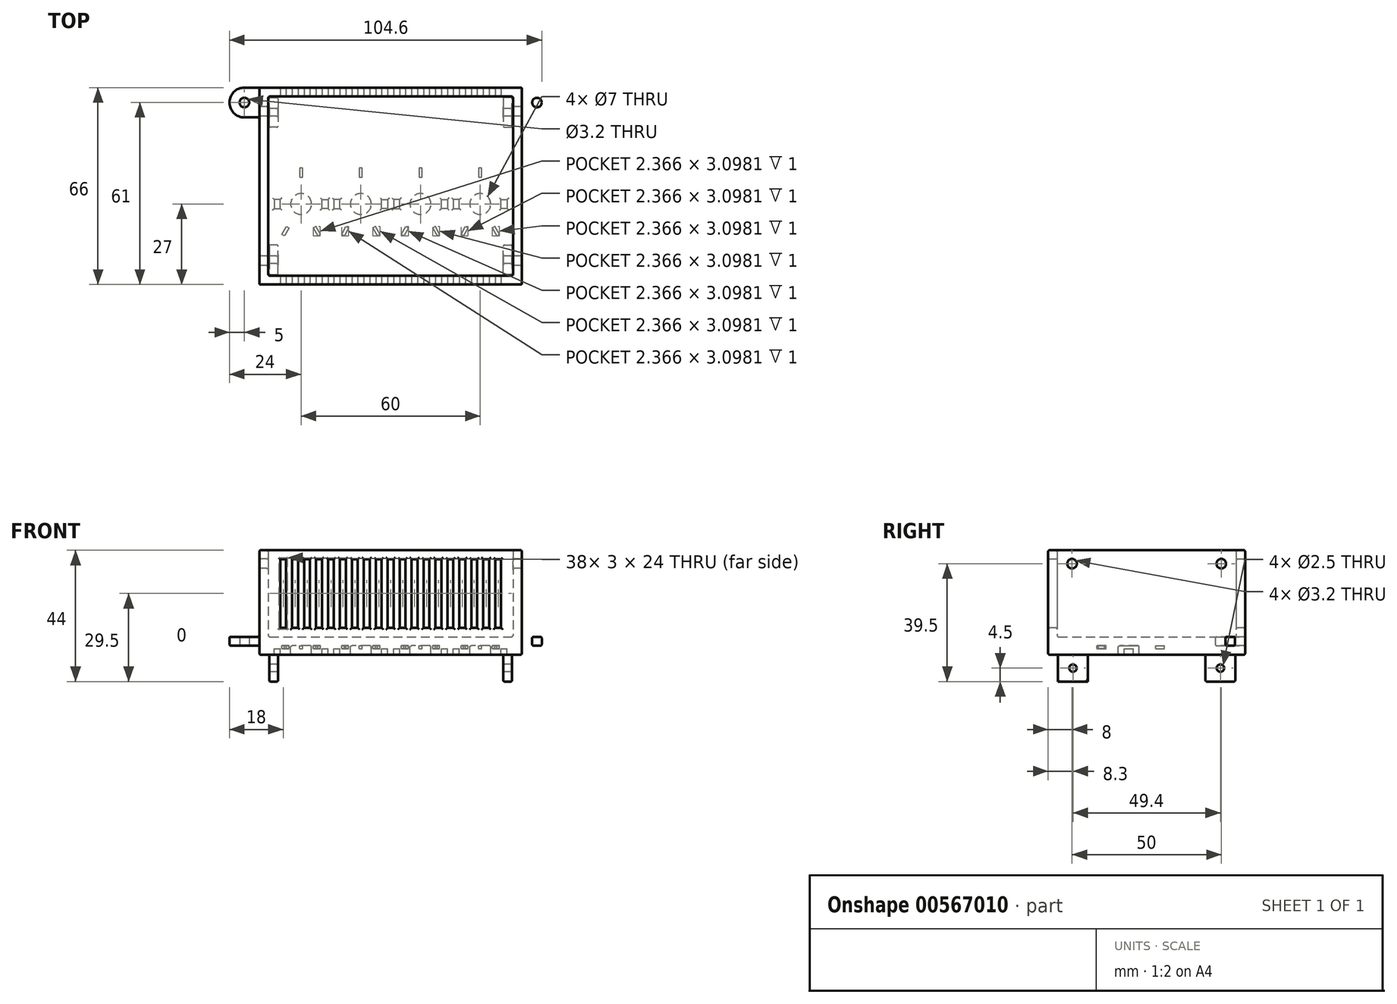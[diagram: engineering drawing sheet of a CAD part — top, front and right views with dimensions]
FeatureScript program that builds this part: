
annotation { "Feature Type Name" : "Feature", "Feature Type Description" : "" }
export const myFeature = defineFeature(function(context is Context, id is Id, definition is map)
    precondition{}
    {
        {
            assignVariable(context, id + "F0", {"name" : "wallthickness", "anyValue" : 3 * mm});
        }
        {
            assignVariable(context, id + "F1", {"name" : "width", "anyValue" : 82 * mm});
        }
        {
            assignVariable(context, id + "F2", {"name" : "height", "anyValue" : 60 * mm});
        }
        {
            assignVariable(context, id + "F3", {"name" : "depth", "anyValue" : 29 * mm});
        }
        {
            assignVariable(context, id + "F4", {"name" : "filletrad", "anyValue" : 0.5 * mm});
        }
        {
            var Q0;
            Q0=qCreatedBy(makeId("Top.planeOp"),FACE);
            var sketch = newSketch(context, id + "F5", { "sketchPlane" : qUnion([Q0])});
            skLineSegment(sketch, "E0", {"start": v(0, 0) * mm, "end": v(82, 0) * mm});
            skLineSegment(sketch, "E1", {"start": v(82, 0) * mm, "end": v(82, -60) * mm});
            skLineSegment(sketch, "E2", {"start": v(82, -60) * mm, "end": v(0, -60) * mm});
            skLineSegment(sketch, "E3", {"start": v(0, -60) * mm, "end": v(0, 0) * mm});
            skLineSegment(sketch, "E4.0", {"start": v(-3, 3) * mm, "end": v(85, 3) * mm});
            skLineSegment(sketch, "E4.1", {"start": v(-3, -63) * mm, "end": v(-3, 3) * mm});
            skLineSegment(sketch, "E4.2", {"start": v(85, -63) * mm, "end": v(-3, -63) * mm});
            skLineSegment(sketch, "E4.3", {"start": v(85, 3) * mm, "end": v(85, -63) * mm});
            skLineSegment(sketch, "E5", {"start": v(0.3, -0.3) * mm, "end": v(3.3, -0.3) * mm});
            skLineSegment(sketch, "E6", {"start": v(3.3, -0.3) * mm, "end": v(3.3, -10.3) * mm});
            skLineSegment(sketch, "E7", {"start": v(3.3, -10.3) * mm, "end": v(0.3, -10.3) * mm});
            skLineSegment(sketch, "E8", {"start": v(0.3, -10.3) * mm, "end": v(0.3, -0.3) * mm});
            skLineSegment(sketch, "E9", {"start": v(-3, -30) * mm, "end": v(85, -30) * mm, "construction": true});
            skLineSegment(sketch, "E10.MirrorCS", {"start": v(3.3, -59.7) * mm, "end": v(3.3, -49.7) * mm});
            skLineSegment(sketch, "E11.MirrorCS", {"start": v(3.3, -49.7) * mm, "end": v(0.3, -49.7) * mm});
            skLineSegment(sketch, "E12.MirrorCS", {"start": v(0.3, -59.7) * mm, "end": v(3.3, -59.7) * mm});
            skLineSegment(sketch, "E13.MirrorCS", {"start": v(0.3, -49.7) * mm, "end": v(0.3, -59.7) * mm});
            skCircle(sketch, "E14", {"center": v(11, -36) * mm, "radius": 9 * mm, "construction": true});
            skCircle(sketch, "E15", {"center": v(11, -36) * mm, "radius": 3.5 * mm});
            skLineSegment(sketch, "E16", {"start": v(18, -34.5) * mm, "end": v(20, -34.5) * mm});
            skLineSegment(sketch, "E17", {"start": v(20, -34.5) * mm, "end": v(20, -37.5) * mm});
            skLineSegment(sketch, "E18", {"start": v(20, -37.5) * mm, "end": v(18, -37.5) * mm});
            skLineSegment(sketch, "E19", {"start": v(18, -37.5) * mm, "end": v(18, -34.5) * mm});
            skLineSegment(sketch, "E20", {"start": v(11, -36) * mm, "end": v(11, -30) * mm, "construction": true});
            skLineSegment(sketch, "E21.MirrorCS", {"start": v(2, -37.5) * mm, "end": v(4, -37.5) * mm});
            skLineSegment(sketch, "E22.MirrorCS", {"start": v(2, -34.5) * mm, "end": v(2, -37.5) * mm});
            skLineSegment(sketch, "E23.MirrorCS", {"start": v(4, -37.5) * mm, "end": v(4, -34.5) * mm});
            skLineSegment(sketch, "E24.MirrorCS", {"start": v(4, -34.5) * mm, "end": v(2, -34.5) * mm});
            skLineSegment(sketch, "E25.1.0.0", {"start": v(22, -37.5) * mm, "end": v(24, -37.5) * mm});
            skLineSegment(sketch, "E25.1.0.1", {"start": v(22, -34.5) * mm, "end": v(22, -37.5) * mm});
            skLineSegment(sketch, "E25.1.0.2", {"start": v(24, -34.5) * mm, "end": v(22, -34.5) * mm});
            skLineSegment(sketch, "E25.1.0.3", {"start": v(24, -37.5) * mm, "end": v(24, -34.5) * mm});
            skLineSegment(sketch, "E25.1.0.4", {"start": v(40, -34.5) * mm, "end": v(40, -37.5) * mm});
            skCircle(sketch, "E25.1.0.5", {"center": v(31, -36) * mm, "radius": 3.5 * mm});
            skLineSegment(sketch, "E25.1.0.6", {"start": v(38, -34.5) * mm, "end": v(40, -34.5) * mm});
            skLineSegment(sketch, "E25.1.0.7", {"start": v(38, -37.5) * mm, "end": v(38, -34.5) * mm});
            skLineSegment(sketch, "E25.1.0.8", {"start": v(31, -36) * mm, "end": v(31, -30) * mm, "construction": true});
            skLineSegment(sketch, "E25.1.0.9", {"start": v(40, -37.5) * mm, "end": v(38, -37.5) * mm});
            skLineSegment(sketch, "E25.2.0.0", {"start": v(42, -37.5) * mm, "end": v(44, -37.5) * mm});
            skLineSegment(sketch, "E25.2.0.1", {"start": v(42, -34.5) * mm, "end": v(42, -37.5) * mm});
            skLineSegment(sketch, "E25.2.0.2", {"start": v(44, -34.5) * mm, "end": v(42, -34.5) * mm});
            skLineSegment(sketch, "E25.2.0.3", {"start": v(44, -37.5) * mm, "end": v(44, -34.5) * mm});
            skLineSegment(sketch, "E25.2.0.4", {"start": v(60, -34.5) * mm, "end": v(60, -37.5) * mm});
            skCircle(sketch, "E25.2.0.5", {"center": v(51, -36) * mm, "radius": 3.5 * mm});
            skLineSegment(sketch, "E25.2.0.6", {"start": v(58, -34.5) * mm, "end": v(60, -34.5) * mm});
            skLineSegment(sketch, "E25.2.0.7", {"start": v(58, -37.5) * mm, "end": v(58, -34.5) * mm});
            skLineSegment(sketch, "E25.2.0.8", {"start": v(51, -36) * mm, "end": v(51, -30) * mm, "construction": true});
            skLineSegment(sketch, "E25.2.0.9", {"start": v(60, -37.5) * mm, "end": v(58, -37.5) * mm});
            skLineSegment(sketch, "E25.3.0.0", {"start": v(62, -37.5) * mm, "end": v(64, -37.5) * mm});
            skLineSegment(sketch, "E25.3.0.1", {"start": v(62, -34.5) * mm, "end": v(62, -37.5) * mm});
            skLineSegment(sketch, "E25.3.0.2", {"start": v(64, -34.5) * mm, "end": v(62, -34.5) * mm});
            skLineSegment(sketch, "E25.3.0.3", {"start": v(64, -37.5) * mm, "end": v(64, -34.5) * mm});
            skLineSegment(sketch, "E25.3.0.4", {"start": v(80, -34.5) * mm, "end": v(80, -37.5) * mm});
            skCircle(sketch, "E25.3.0.5", {"center": v(71, -36) * mm, "radius": 3.5 * mm});
            skLineSegment(sketch, "E25.3.0.6", {"start": v(78, -34.5) * mm, "end": v(80, -34.5) * mm});
            skLineSegment(sketch, "E25.3.0.7", {"start": v(78, -37.5) * mm, "end": v(78, -34.5) * mm});
            skLineSegment(sketch, "E25.3.0.8", {"start": v(71, -36) * mm, "end": v(71, -30) * mm, "construction": true});
            skLineSegment(sketch, "E25.3.0.9", {"start": v(80, -37.5) * mm, "end": v(78, -37.5) * mm});
            skLineSegment(sketch, "E25.direction1", {"start": v(2, -37.5) * mm, "end": v(22, -37.5) * mm, "construction": true});
            skLineSegment(sketch, "E26", {"start": v(41, 3) * mm, "end": v(41, -60) * mm, "construction": true});
            skLineSegment(sketch, "E27.MirrorCS", {"start": v(81.7, -49.7) * mm, "end": v(81.7, -59.7) * mm});
            skLineSegment(sketch, "E28.MirrorCS", {"start": v(78.7, -49.7) * mm, "end": v(81.7, -49.7) * mm});
            skLineSegment(sketch, "E29.MirrorCS", {"start": v(81.7, -59.7) * mm, "end": v(78.7, -59.7) * mm});
            skLineSegment(sketch, "E30.MirrorCS", {"start": v(78.7, -59.7) * mm, "end": v(78.7, -49.7) * mm});
            skLineSegment(sketch, "E31.MirrorCS", {"start": v(81.7, -10.3) * mm, "end": v(81.7, -0.3) * mm});
            skLineSegment(sketch, "E32.MirrorCS", {"start": v(78.7, -0.3) * mm, "end": v(78.7, -10.3) * mm});
            skLineSegment(sketch, "E33.MirrorCS", {"start": v(81.7, -0.3) * mm, "end": v(78.7, -0.3) * mm});
            skLineSegment(sketch, "E34.MirrorCS", {"start": v(78.7, -10.3) * mm, "end": v(81.7, -10.3) * mm});
            skLineSegment(sketch, "E35", {"start": v(11, -36) * mm, "end": v(5, -46.4) * mm, "construction": true});
            skLineSegment(sketch, "E36", {"start": v(5, -46.4) * mm, "end": v(4.57, -46.14) * mm});
            skLineSegment(sketch, "E37", {"start": v(4.57, -46.14) * mm, "end": v(6.07, -43.54) * mm});
            skLineSegment(sketch, "E38", {"start": v(6.07, -43.54) * mm, "end": v(6.93, -44.04) * mm});
            skLineSegment(sketch, "E39", {"start": v(6.93, -44.04) * mm, "end": v(5.43, -46.64) * mm});
            skLineSegment(sketch, "E40", {"start": v(5.43, -46.64) * mm, "end": v(5, -46.4) * mm});
            skLineSegment(sketch, "E41.MirrorCS", {"start": v(16.57, -46.64) * mm, "end": v(17, -46.4) * mm});
            skLineSegment(sketch, "E42.MirrorCS", {"start": v(17, -46.4) * mm, "end": v(17.43, -46.14) * mm});
            skLineSegment(sketch, "E43.MirrorCS", {"start": v(15.07, -44.04) * mm, "end": v(16.57, -46.64) * mm});
            skLineSegment(sketch, "E44.MirrorCS", {"start": v(15.93, -43.54) * mm, "end": v(15.07, -44.04) * mm});
            skLineSegment(sketch, "E45.MirrorCS", {"start": v(17.43, -46.14) * mm, "end": v(15.93, -43.54) * mm});
            skLineSegment(sketch, "E46", {"start": v(11, -30) * mm, "end": v(11, -27) * mm, "construction": true});
            skLineSegment(sketch, "E47", {"start": v(11, -27) * mm, "end": v(11.5, -27) * mm});
            skLineSegment(sketch, "E48", {"start": v(11.5, -27) * mm, "end": v(11.5, -24) * mm});
            skLineSegment(sketch, "E49", {"start": v(11.5, -24) * mm, "end": v(10.5, -24) * mm});
            skLineSegment(sketch, "E50", {"start": v(10.5, -24) * mm, "end": v(10.5, -27) * mm});
            skLineSegment(sketch, "E51", {"start": v(10.5, -27) * mm, "end": v(11, -27) * mm});
            skLineSegment(sketch, "E52.1.0.0", {"start": v(31.5, -27) * mm, "end": v(31.5, -24) * mm});
            skLineSegment(sketch, "E52.1.0.1", {"start": v(30.5, -27) * mm, "end": v(31, -27) * mm});
            skLineSegment(sketch, "E52.1.0.2", {"start": v(30.5, -24) * mm, "end": v(30.5, -27) * mm});
            skLineSegment(sketch, "E52.1.0.3", {"start": v(31, -27) * mm, "end": v(31.5, -27) * mm});
            skLineSegment(sketch, "E52.1.0.4", {"start": v(31.5, -24) * mm, "end": v(30.5, -24) * mm});
            skLineSegment(sketch, "E52.1.0.5", {"start": v(37.43, -46.14) * mm, "end": v(35.93, -43.54) * mm});
            skLineSegment(sketch, "E52.1.0.6", {"start": v(35.07, -44.04) * mm, "end": v(36.57, -46.64) * mm});
            skLineSegment(sketch, "E52.1.0.7", {"start": v(26.93, -44.04) * mm, "end": v(25.43, -46.64) * mm});
            skLineSegment(sketch, "E52.1.0.8", {"start": v(24.57, -46.14) * mm, "end": v(26.07, -43.54) * mm});
            skLineSegment(sketch, "E52.1.0.9", {"start": v(36.57, -46.64) * mm, "end": v(37, -46.4) * mm});
            skLineSegment(sketch, "E52.1.0.10", {"start": v(35.93, -43.54) * mm, "end": v(35.07, -44.04) * mm});
            skLineSegment(sketch, "E52.1.0.11", {"start": v(37, -46.4) * mm, "end": v(37.43, -46.14) * mm});
            skLineSegment(sketch, "E52.1.0.12", {"start": v(26.07, -43.54) * mm, "end": v(26.93, -44.04) * mm});
            skLineSegment(sketch, "E52.1.0.13", {"start": v(25.43, -46.64) * mm, "end": v(25, -46.4) * mm});
            skLineSegment(sketch, "E52.1.0.14", {"start": v(25, -46.4) * mm, "end": v(24.57, -46.14) * mm});
            skLineSegment(sketch, "E52.2.0.0", {"start": v(51.5, -27) * mm, "end": v(51.5, -24) * mm});
            skLineSegment(sketch, "E52.2.0.1", {"start": v(50.5, -27) * mm, "end": v(51, -27) * mm});
            skLineSegment(sketch, "E52.2.0.2", {"start": v(50.5, -24) * mm, "end": v(50.5, -27) * mm});
            skLineSegment(sketch, "E52.2.0.3", {"start": v(51, -27) * mm, "end": v(51.5, -27) * mm});
            skLineSegment(sketch, "E52.2.0.4", {"start": v(51.5, -24) * mm, "end": v(50.5, -24) * mm});
            skLineSegment(sketch, "E52.2.0.5", {"start": v(57.43, -46.14) * mm, "end": v(55.93, -43.54) * mm});
            skLineSegment(sketch, "E52.2.0.6", {"start": v(55.07, -44.04) * mm, "end": v(56.57, -46.64) * mm});
            skLineSegment(sketch, "E52.2.0.7", {"start": v(46.93, -44.04) * mm, "end": v(45.43, -46.64) * mm});
            skLineSegment(sketch, "E52.2.0.8", {"start": v(44.57, -46.14) * mm, "end": v(46.07, -43.54) * mm});
            skLineSegment(sketch, "E52.2.0.9", {"start": v(56.57, -46.64) * mm, "end": v(57, -46.4) * mm});
            skLineSegment(sketch, "E52.2.0.10", {"start": v(55.93, -43.54) * mm, "end": v(55.07, -44.04) * mm});
            skLineSegment(sketch, "E52.2.0.11", {"start": v(57, -46.4) * mm, "end": v(57.43, -46.14) * mm});
            skLineSegment(sketch, "E52.2.0.12", {"start": v(46.07, -43.54) * mm, "end": v(46.93, -44.04) * mm});
            skLineSegment(sketch, "E52.2.0.13", {"start": v(45.43, -46.64) * mm, "end": v(45, -46.4) * mm});
            skLineSegment(sketch, "E52.2.0.14", {"start": v(45, -46.4) * mm, "end": v(44.57, -46.14) * mm});
            skLineSegment(sketch, "E52.3.0.0", {"start": v(71.5, -27) * mm, "end": v(71.5, -24) * mm});
            skLineSegment(sketch, "E52.3.0.1", {"start": v(70.5, -27) * mm, "end": v(71, -27) * mm});
            skLineSegment(sketch, "E52.3.0.2", {"start": v(70.5, -24) * mm, "end": v(70.5, -27) * mm});
            skLineSegment(sketch, "E52.3.0.3", {"start": v(71, -27) * mm, "end": v(71.5, -27) * mm});
            skLineSegment(sketch, "E52.3.0.4", {"start": v(71.5, -24) * mm, "end": v(70.5, -24) * mm});
            skLineSegment(sketch, "E52.3.0.5", {"start": v(77.43, -46.14) * mm, "end": v(75.93, -43.54) * mm});
            skLineSegment(sketch, "E52.3.0.6", {"start": v(75.07, -44.04) * mm, "end": v(76.57, -46.64) * mm});
            skLineSegment(sketch, "E52.3.0.7", {"start": v(66.93, -44.04) * mm, "end": v(65.43, -46.64) * mm});
            skLineSegment(sketch, "E52.3.0.8", {"start": v(64.57, -46.14) * mm, "end": v(66.07, -43.54) * mm});
            skLineSegment(sketch, "E52.3.0.9", {"start": v(76.57, -46.64) * mm, "end": v(77, -46.4) * mm});
            skLineSegment(sketch, "E52.3.0.10", {"start": v(75.93, -43.54) * mm, "end": v(75.07, -44.04) * mm});
            skLineSegment(sketch, "E52.3.0.11", {"start": v(77, -46.4) * mm, "end": v(77.43, -46.14) * mm});
            skLineSegment(sketch, "E52.3.0.12", {"start": v(66.07, -43.54) * mm, "end": v(66.93, -44.04) * mm});
            skLineSegment(sketch, "E52.3.0.13", {"start": v(65.43, -46.64) * mm, "end": v(65, -46.4) * mm});
            skLineSegment(sketch, "E52.3.0.14", {"start": v(65, -46.4) * mm, "end": v(64.57, -46.14) * mm});
            skLineSegment(sketch, "E52.direction1", {"start": v(4.57, -46.14) * mm, "end": v(24.57, -46.14) * mm, "construction": true});
            skLineSegment(sketch, "E53", {"start": v(-3, 3) * mm, "end": v(-8, 3) * mm});
            skLineSegment(sketch, "E54", {"start": v(-8, 3) * mm, "end": v(-8, -7) * mm, "construction": true});
            skLineSegment(sketch, "E55", {"start": v(-8, -7) * mm, "end": v(-3, -7) * mm});
            skArc(sketch, "E56", {"start": v(-8, 3) * mm, "mid": v(-13, -2) * mm, "end": v(-8, -7) * mm});
            skCircle(sketch, "E57", {"center": v(-8, -2) * mm, "radius": 1.6 * mm});
            skCircle(sketch, "E58.MirrorC", {"center": v(90, -2) * mm, "radius": 1.6 * mm});
            skArc(sketch, "E59.MirrorCS", {"start": v(90, 3) * mm, "mid": v(95, -2) * mm, "end": v(90, -7) * mm});
            skLineSegment(sketch, "E60.MirrorCS", {"start": v(90, -7) * mm, "end": v(85, -7) * mm});
            skLineSegment(sketch, "E61.MirrorCS", {"start": v(85, 3) * mm, "end": v(90, 3) * mm});
            skLineSegment(sketch, "E62.MirrorCS", {"start": v(90, 3) * mm, "end": v(90, -7) * mm, "construction": true});
            skSolve(sketch);
        }
        {
            var Q0;
            Q0=makeQuery(id+"F5.imprint","IMPRINT",FACE,{"disambiguationData":[TD([[makeQuery(id+"F5.imprint","IMPRINT",EDGE,{"derivedFrom":sQuery(id+"F5.wireOp",EDGE,"E0")}),1.0]])]});
            extrude(context, id + "F6", {"entities" : qUnion([Q0]), "depth" : getVariable(context, 'depth') + getVariable(context, 'wallthickness'), "offsetDistance" : 25 * mm});
        }
        {
            var Q0;
            Q0=makeQuery(id+"F5.imprint","IMPRINT",FACE,{"disambiguationData":[TD([[makeQuery(id+"F5.imprint","IMPRINT",EDGE,{"derivedFrom":sQuery(id+"F5.wireOp",EDGE,"E0")}),-1.0]])]});
            var Q1;
            Q1=makeQuery(id+"F5.imprint","IMPRINT",FACE,{"disambiguationData":[TD([[makeQuery(id+"F5.imprint","IMPRINT",EDGE,{"derivedFrom":sQuery(id+"F5.wireOp",EDGE,"E5")}),-1.0]])]});
            var Q2;
            Q2=makeQuery(id+"F5.imprint","IMPRINT",FACE,{"disambiguationData":[TD([[makeQuery(id+"F5.imprint","IMPRINT",EDGE,{"derivedFrom":sQuery(id+"F5.wireOp",EDGE,"E10.MirrorCS")}),1.0]])]});
            var Q3;
            Q3=makeQuery(id+"F5.imprint","IMPRINT",FACE,{"disambiguationData":[TD([[makeQuery(id+"F5.imprint","IMPRINT",EDGE,{"derivedFrom":sQuery(id+"F5.wireOp",EDGE,"E21.MirrorCS")}),1.0]])]});
            var Q4;
            Q4=makeQuery(id+"F5.imprint","IMPRINT",FACE,{"disambiguationData":[TD([[makeQuery(id+"F5.imprint","IMPRINT",EDGE,{"derivedFrom":sQuery(id+"F5.wireOp",EDGE,"E15")}),1.0]])]});
            var Q5;
            Q5=makeQuery(id+"F5.imprint","IMPRINT",FACE,{"disambiguationData":[TD([[makeQuery(id+"F5.imprint","IMPRINT",EDGE,{"derivedFrom":sQuery(id+"F5.wireOp",EDGE,"E16")}),-1.0]])]});
            var Q6;
            Q6=makeQuery(id+"F5.imprint","IMPRINT",FACE,{"disambiguationData":[TD([[makeQuery(id+"F5.imprint","IMPRINT",EDGE,{"derivedFrom":sQuery(id+"F5.wireOp",EDGE,"E25.1.0.0")}),1.0]])]});
            var Q7;
            Q7=makeQuery(id+"F5.imprint","IMPRINT",FACE,{"disambiguationData":[TD([[makeQuery(id+"F5.imprint","IMPRINT",EDGE,{"derivedFrom":sQuery(id+"F5.wireOp",EDGE,"E25.1.0.5")}),1.0]])]});
            var Q8;
            Q8=makeQuery(id+"F5.imprint","IMPRINT",FACE,{"disambiguationData":[TD([[makeQuery(id+"F5.imprint","IMPRINT",EDGE,{"derivedFrom":sQuery(id+"F5.wireOp",EDGE,"E25.1.0.4")}),-1.0]])]});
            var Q9;
            Q9=makeQuery(id+"F5.imprint","IMPRINT",FACE,{"disambiguationData":[TD([[makeQuery(id+"F5.imprint","IMPRINT",EDGE,{"derivedFrom":sQuery(id+"F5.wireOp",EDGE,"E25.2.0.0")}),1.0]])]});
            var Q10;
            Q10=makeQuery(id+"F5.imprint","IMPRINT",FACE,{"disambiguationData":[TD([[makeQuery(id+"F5.imprint","IMPRINT",EDGE,{"derivedFrom":sQuery(id+"F5.wireOp",EDGE,"E25.2.0.5")}),1.0]])]});
            var Q11;
            Q11=makeQuery(id+"F5.imprint","IMPRINT",FACE,{"disambiguationData":[TD([[makeQuery(id+"F5.imprint","IMPRINT",EDGE,{"derivedFrom":sQuery(id+"F5.wireOp",EDGE,"E25.3.0.0")}),1.0]])]});
            var Q12;
            Q12=makeQuery(id+"F5.imprint","IMPRINT",FACE,{"disambiguationData":[TD([[makeQuery(id+"F5.imprint","IMPRINT",EDGE,{"derivedFrom":sQuery(id+"F5.wireOp",EDGE,"E25.2.0.4")}),-1.0]])]});
            var Q13;
            Q13=makeQuery(id+"F5.imprint","IMPRINT",FACE,{"disambiguationData":[TD([[makeQuery(id+"F5.imprint","IMPRINT",EDGE,{"derivedFrom":sQuery(id+"F5.wireOp",EDGE,"E25.3.0.5")}),1.0]])]});
            var Q14;
            Q14=makeQuery(id+"F5.imprint","IMPRINT",FACE,{"disambiguationData":[TD([[makeQuery(id+"F5.imprint","IMPRINT",EDGE,{"derivedFrom":sQuery(id+"F5.wireOp",EDGE,"E25.3.0.4")}),-1.0]])]});
            var Q15;
            Q15=makeQuery(id+"F5.imprint","IMPRINT",FACE,{"disambiguationData":[TD([[makeQuery(id+"F5.imprint","IMPRINT",EDGE,{"derivedFrom":sQuery(id+"F5.wireOp",EDGE,"E31.MirrorCS")}),1.0]])]});
            var Q16;
            Q16=makeQuery(id+"F5.imprint","IMPRINT",FACE,{"disambiguationData":[TD([[makeQuery(id+"F5.imprint","IMPRINT",EDGE,{"derivedFrom":sQuery(id+"F5.wireOp",EDGE,"E27.MirrorCS")}),-1.0]])]});
            var Q17;
            Q17=makeQuery(id+"F5.imprint","IMPRINT",FACE,{"disambiguationData":[TD([[makeQuery(id+"F5.imprint","IMPRINT",EDGE,{"derivedFrom":sQuery(id+"F5.wireOp",EDGE,"E36")}),-1.0]])]});
            var Q18;
            Q18=makeQuery(id+"F5.imprint","IMPRINT",FACE,{"disambiguationData":[TD([[makeQuery(id+"F5.imprint","IMPRINT",EDGE,{"derivedFrom":sQuery(id+"F5.wireOp",EDGE,"E41.MirrorCS")}),1.0]])]});
            var Q19;
            Q19=makeQuery(id+"F5.imprint","IMPRINT",FACE,{"disambiguationData":[TD([[makeQuery(id+"F5.imprint","IMPRINT",EDGE,{"derivedFrom":sQuery(id+"F5.wireOp",EDGE,"E47")}),1.0]])]});
            var Q20;
            Q20=makeQuery(id+"F5.imprint","IMPRINT",FACE,{"disambiguationData":[TD([[makeQuery(id+"F5.imprint","IMPRINT",EDGE,{"derivedFrom":sQuery(id+"F5.wireOp",EDGE,"E52.1.0.5")}),1.0]])]});
            var Q21;
            Q21=makeQuery(id+"F5.imprint","IMPRINT",FACE,{"disambiguationData":[TD([[makeQuery(id+"F5.imprint","IMPRINT",EDGE,{"derivedFrom":sQuery(id+"F5.wireOp",EDGE,"E52.2.0.0")}),1.0]])]});
            var Q22;
            Q22=makeQuery(id+"F5.imprint","IMPRINT",FACE,{"disambiguationData":[TD([[makeQuery(id+"F5.imprint","IMPRINT",EDGE,{"derivedFrom":sQuery(id+"F5.wireOp",EDGE,"E52.2.0.7")}),-1.0]])]});
            var Q23;
            Q23=makeQuery(id+"F5.imprint","IMPRINT",FACE,{"disambiguationData":[TD([[makeQuery(id+"F5.imprint","IMPRINT",EDGE,{"derivedFrom":sQuery(id+"F5.wireOp",EDGE,"E52.2.0.5")}),1.0]])]});
            var Q24;
            Q24=makeQuery(id+"F5.imprint","IMPRINT",FACE,{"disambiguationData":[TD([[makeQuery(id+"F5.imprint","IMPRINT",EDGE,{"derivedFrom":sQuery(id+"F5.wireOp",EDGE,"E52.3.0.0")}),1.0]])]});
            var Q25;
            Q25=makeQuery(id+"F5.imprint","IMPRINT",FACE,{"disambiguationData":[TD([[makeQuery(id+"F5.imprint","IMPRINT",EDGE,{"derivedFrom":sQuery(id+"F5.wireOp",EDGE,"E52.3.0.7")}),-1.0]])]});
            var Q26;
            Q26=makeQuery(id+"F5.imprint","IMPRINT",FACE,{"disambiguationData":[TD([[makeQuery(id+"F5.imprint","IMPRINT",EDGE,{"derivedFrom":sQuery(id+"F5.wireOp",EDGE,"E52.3.0.5")}),1.0]])]});
            var Q27;
            Q27=makeQuery(id+"F5.imprint","IMPRINT",FACE,{"disambiguationData":[TD([[makeQuery(id+"F5.imprint","IMPRINT",EDGE,{"derivedFrom":sQuery(id+"F5.wireOp",EDGE,"E52.1.0.0")}),1.0]])]});
            var Q28;
            Q28=makeQuery(id+"F5.imprint","IMPRINT",FACE,{"disambiguationData":[TD([[makeQuery(id+"F5.imprint","IMPRINT",EDGE,{"derivedFrom":sQuery(id+"F5.wireOp",EDGE,"E52.1.0.7")}),-1.0]])]});
            var Q29;
            {var subQ1=sQuery(id+"F5.wireOp",EDGE,"E53");Q29=makeQuery(id+"F5.imprint","IMPRINT",FACE,{"disambiguationData":[TD([[makeQuery(id+"F5.imprint","IMPRINT",EDGE,{"derivedFrom":subQ1}),1.0]])]});}
            var Q30;
            Q30=makeQuery(id+"F5.imprint","IMPRINT",FACE,{"disambiguationData":[TD([[makeQuery(id+"F5.imprint","IMPRINT",EDGE,{"derivedFrom":sQuery(id+"F5.wireOp",EDGE,"E58.MirrorC")}),1.0]])]});
            extrude(context, id + "F7", {"entities" : qUnion([Q0, Q1, Q2, Q3, Q4, Q5, Q6, Q7, Q8, Q9, Q10, Q11, Q12, Q13, Q14, Q15, Q16, Q17, Q18, Q19, Q20, Q21, Q22, Q23, Q24, Q25, Q26, Q27, Q28, Q29, Q30]), "operationType" : NewBodyOperationType.ADD, "depth" : getVariable(context, 'wallthickness'), "offsetDistance" : 25 * mm});
        }
        {
            var Q0;
            Q0=makeQuery(id+"F5.imprint","IMPRINT",FACE,{"disambiguationData":[TD([[makeQuery(id+"F5.imprint","IMPRINT",EDGE,{"derivedFrom":sQuery(id+"F5.wireOp",EDGE,"E0")}),1.0]])]});
            var Q1;
            Q1=makeQuery(id+"F5.imprint","IMPRINT",FACE,{"disambiguationData":[TD([[makeQuery(id+"F5.imprint","IMPRINT",EDGE,{"derivedFrom":sQuery(id+"F5.wireOp",EDGE,"E0")}),-1.0]])]});
            var Q2;
            Q2=makeQuery(id+"F5.imprint","IMPRINT",FACE,{"disambiguationData":[TD([[makeQuery(id+"F5.imprint","IMPRINT",EDGE,{"derivedFrom":sQuery(id+"F5.wireOp",EDGE,"E5")}),-1.0]])]});
            var Q3;
            Q3=makeQuery(id+"F5.imprint","IMPRINT",FACE,{"disambiguationData":[TD([[makeQuery(id+"F5.imprint","IMPRINT",EDGE,{"derivedFrom":sQuery(id+"F5.wireOp",EDGE,"E10.MirrorCS")}),1.0]])]});
            var Q4;
            Q4=makeQuery(id+"F5.imprint","IMPRINT",FACE,{"disambiguationData":[TD([[makeQuery(id+"F5.imprint","IMPRINT",EDGE,{"derivedFrom":sQuery(id+"F5.wireOp",EDGE,"E31.MirrorCS")}),1.0]])]});
            var Q5;
            Q5=makeQuery(id+"F5.imprint","IMPRINT",FACE,{"disambiguationData":[TD([[makeQuery(id+"F5.imprint","IMPRINT",EDGE,{"derivedFrom":sQuery(id+"F5.wireOp",EDGE,"E27.MirrorCS")}),-1.0]])]});
            var Q6;
            Q6=makeQuery(id+"F5.imprint","IMPRINT",FACE,{"disambiguationData":[TD([[makeQuery(id+"F5.imprint","IMPRINT",EDGE,{"derivedFrom":sQuery(id+"F5.wireOp",EDGE,"E47")}),1.0]])]});
            var Q7;
            Q7=makeQuery(id+"F5.imprint","IMPRINT",FACE,{"disambiguationData":[TD([[makeQuery(id+"F5.imprint","IMPRINT",EDGE,{"derivedFrom":sQuery(id+"F5.wireOp",EDGE,"E36")}),-1.0]])]});
            var Q8;
            Q8=makeQuery(id+"F5.imprint","IMPRINT",FACE,{"disambiguationData":[TD([[makeQuery(id+"F5.imprint","IMPRINT",EDGE,{"derivedFrom":sQuery(id+"F5.wireOp",EDGE,"E41.MirrorCS")}),1.0]])]});
            var Q9;
            Q9=makeQuery(id+"F5.imprint","IMPRINT",FACE,{"disambiguationData":[TD([[makeQuery(id+"F5.imprint","IMPRINT",EDGE,{"derivedFrom":sQuery(id+"F5.wireOp",EDGE,"E52.1.0.7")}),-1.0]])]});
            var Q10;
            Q10=makeQuery(id+"F5.imprint","IMPRINT",FACE,{"disambiguationData":[TD([[makeQuery(id+"F5.imprint","IMPRINT",EDGE,{"derivedFrom":sQuery(id+"F5.wireOp",EDGE,"E52.1.0.5")}),1.0]])]});
            var Q11;
            Q11=makeQuery(id+"F5.imprint","IMPRINT",FACE,{"disambiguationData":[TD([[makeQuery(id+"F5.imprint","IMPRINT",EDGE,{"derivedFrom":sQuery(id+"F5.wireOp",EDGE,"E52.1.0.0")}),1.0]])]});
            var Q12;
            Q12=makeQuery(id+"F5.imprint","IMPRINT",FACE,{"disambiguationData":[TD([[makeQuery(id+"F5.imprint","IMPRINT",EDGE,{"derivedFrom":sQuery(id+"F5.wireOp",EDGE,"E52.2.0.0")}),1.0]])]});
            var Q13;
            Q13=makeQuery(id+"F5.imprint","IMPRINT",FACE,{"disambiguationData":[TD([[makeQuery(id+"F5.imprint","IMPRINT",EDGE,{"derivedFrom":sQuery(id+"F5.wireOp",EDGE,"E52.2.0.7")}),-1.0]])]});
            var Q14;
            Q14=makeQuery(id+"F5.imprint","IMPRINT",FACE,{"disambiguationData":[TD([[makeQuery(id+"F5.imprint","IMPRINT",EDGE,{"derivedFrom":sQuery(id+"F5.wireOp",EDGE,"E52.2.0.5")}),1.0]])]});
            var Q15;
            Q15=makeQuery(id+"F5.imprint","IMPRINT",FACE,{"disambiguationData":[TD([[makeQuery(id+"F5.imprint","IMPRINT",EDGE,{"derivedFrom":sQuery(id+"F5.wireOp",EDGE,"E52.3.0.7")}),-1.0]])]});
            var Q16;
            Q16=makeQuery(id+"F5.imprint","IMPRINT",FACE,{"disambiguationData":[TD([[makeQuery(id+"F5.imprint","IMPRINT",EDGE,{"derivedFrom":sQuery(id+"F5.wireOp",EDGE,"E52.3.0.5")}),1.0]])]});
            var Q17;
            Q17=makeQuery(id+"F5.imprint","IMPRINT",FACE,{"disambiguationData":[TD([[makeQuery(id+"F5.imprint","IMPRINT",EDGE,{"derivedFrom":sQuery(id+"F5.wireOp",EDGE,"E52.3.0.0")}),1.0]])]});
            extrude(context, id + "F8", {"entities" : qUnion([Q0, Q1, Q2, Q3, Q4, Q5, Q6, Q7, Q8, Q9, Q10, Q11, Q12, Q13, Q14, Q15, Q16, Q17]), "oppositeDirection" : true, "depth" : getVariable(context, 'wallthickness'), "offsetDistance" : 25 * mm});
        }
        {
            var Q0;
            Q0=makeQuery(id+"F5.imprint","IMPRINT",FACE,{"disambiguationData":[TD([[makeQuery(id+"F5.imprint","IMPRINT",EDGE,{"derivedFrom":sQuery(id+"F5.wireOp",EDGE,"E21.MirrorCS")}),1.0]])]});
            var Q1;
            Q1=makeQuery(id+"F5.imprint","IMPRINT",FACE,{"disambiguationData":[TD([[makeQuery(id+"F5.imprint","IMPRINT",EDGE,{"derivedFrom":sQuery(id+"F5.wireOp",EDGE,"E16")}),-1.0]])]});
            var Q2;
            Q2=makeQuery(id+"F5.imprint","IMPRINT",FACE,{"disambiguationData":[TD([[makeQuery(id+"F5.imprint","IMPRINT",EDGE,{"derivedFrom":sQuery(id+"F5.wireOp",EDGE,"E25.1.0.0")}),1.0]])]});
            var Q3;
            Q3=makeQuery(id+"F5.imprint","IMPRINT",FACE,{"disambiguationData":[TD([[makeQuery(id+"F5.imprint","IMPRINT",EDGE,{"derivedFrom":sQuery(id+"F5.wireOp",EDGE,"E25.1.0.4")}),-1.0]])]});
            var Q4;
            Q4=makeQuery(id+"F5.imprint","IMPRINT",FACE,{"disambiguationData":[TD([[makeQuery(id+"F5.imprint","IMPRINT",EDGE,{"derivedFrom":sQuery(id+"F5.wireOp",EDGE,"E25.2.0.0")}),1.0]])]});
            var Q5;
            Q5=makeQuery(id+"F5.imprint","IMPRINT",FACE,{"disambiguationData":[TD([[makeQuery(id+"F5.imprint","IMPRINT",EDGE,{"derivedFrom":sQuery(id+"F5.wireOp",EDGE,"E25.2.0.4")}),-1.0]])]});
            var Q6;
            Q6=makeQuery(id+"F5.imprint","IMPRINT",FACE,{"disambiguationData":[TD([[makeQuery(id+"F5.imprint","IMPRINT",EDGE,{"derivedFrom":sQuery(id+"F5.wireOp",EDGE,"E25.3.0.0")}),1.0]])]});
            var Q7;
            Q7=makeQuery(id+"F5.imprint","IMPRINT",FACE,{"disambiguationData":[TD([[makeQuery(id+"F5.imprint","IMPRINT",EDGE,{"derivedFrom":sQuery(id+"F5.wireOp",EDGE,"E25.3.0.4")}),-1.0]])]});
            extrude(context, id + "F9", {"entities" : qUnion([Q0, Q1, Q2, Q3, Q4, Q5, Q6, Q7]), "operationType" : NewBodyOperationType.ADD, "oppositeDirection" : true, "depth" : 1 * mm, "offsetDistance" : 25 * mm});
        }
        {
            var Q0;
            Q0=makeQuery(id+"F5.imprint","IMPRINT",FACE,{"disambiguationData":[TD([[makeQuery(id+"F5.imprint","IMPRINT",EDGE,{"derivedFrom":sQuery(id+"F5.wireOp",EDGE,"E5")}),-1.0]])]});
            var Q1;
            Q1=makeQuery(id+"F5.imprint","IMPRINT",FACE,{"disambiguationData":[TD([[makeQuery(id+"F5.imprint","IMPRINT",EDGE,{"derivedFrom":sQuery(id+"F5.wireOp",EDGE,"E10.MirrorCS")}),1.0]])]});
            var Q2;
            Q2=makeQuery(id+"F5.imprint","IMPRINT",FACE,{"disambiguationData":[TD([[makeQuery(id+"F5.imprint","IMPRINT",EDGE,{"derivedFrom":sQuery(id+"F5.wireOp",EDGE,"E31.MirrorCS")}),1.0]])]});
            var Q3;
            Q3=makeQuery(id+"F5.imprint","IMPRINT",FACE,{"disambiguationData":[TD([[makeQuery(id+"F5.imprint","IMPRINT",EDGE,{"derivedFrom":sQuery(id+"F5.wireOp",EDGE,"E27.MirrorCS")}),-1.0]])]});
            extrude(context, id + "F10", {"entities" : qUnion([Q0, Q1, Q2, Q3]), "operationType" : NewBodyOperationType.ADD, "oppositeDirection" : true, "depth" : getVariable(context, 'wallthickness') * 4, "offsetDistance" : 25 * mm});
        }
        {
            var Q0;
            Q0=makeQuery(id+"F5.imprint","IMPRINT",FACE,{"disambiguationData":[TD([[makeQuery(id+"F5.imprint","IMPRINT",EDGE,{"derivedFrom":sQuery(id+"F5.wireOp",EDGE,"E52.3.0.0")}),1.0]])]});
            var Q1;
            Q1=makeQuery(id+"F5.imprint","IMPRINT",FACE,{"disambiguationData":[TD([[makeQuery(id+"F5.imprint","IMPRINT",EDGE,{"derivedFrom":sQuery(id+"F5.wireOp",EDGE,"E52.3.0.7")}),-1.0]])]});
            var Q2;
            Q2=makeQuery(id+"F5.imprint","IMPRINT",FACE,{"disambiguationData":[TD([[makeQuery(id+"F5.imprint","IMPRINT",EDGE,{"derivedFrom":sQuery(id+"F5.wireOp",EDGE,"E52.3.0.5")}),1.0]])]});
            var Q3;
            Q3=makeQuery(id+"F5.imprint","IMPRINT",FACE,{"disambiguationData":[TD([[makeQuery(id+"F5.imprint","IMPRINT",EDGE,{"derivedFrom":sQuery(id+"F5.wireOp",EDGE,"E52.2.0.5")}),1.0]])]});
            var Q4;
            Q4=makeQuery(id+"F5.imprint","IMPRINT",FACE,{"disambiguationData":[TD([[makeQuery(id+"F5.imprint","IMPRINT",EDGE,{"derivedFrom":sQuery(id+"F5.wireOp",EDGE,"E52.2.0.7")}),-1.0]])]});
            var Q5;
            Q5=makeQuery(id+"F5.imprint","IMPRINT",FACE,{"disambiguationData":[TD([[makeQuery(id+"F5.imprint","IMPRINT",EDGE,{"derivedFrom":sQuery(id+"F5.wireOp",EDGE,"E52.2.0.0")}),1.0]])]});
            var Q6;
            Q6=makeQuery(id+"F5.imprint","IMPRINT",FACE,{"disambiguationData":[TD([[makeQuery(id+"F5.imprint","IMPRINT",EDGE,{"derivedFrom":sQuery(id+"F5.wireOp",EDGE,"E52.1.0.5")}),1.0]])]});
            var Q7;
            Q7=makeQuery(id+"F5.imprint","IMPRINT",FACE,{"disambiguationData":[TD([[makeQuery(id+"F5.imprint","IMPRINT",EDGE,{"derivedFrom":sQuery(id+"F5.wireOp",EDGE,"E52.1.0.7")}),-1.0]])]});
            var Q8;
            Q8=makeQuery(id+"F5.imprint","IMPRINT",FACE,{"disambiguationData":[TD([[makeQuery(id+"F5.imprint","IMPRINT",EDGE,{"derivedFrom":sQuery(id+"F5.wireOp",EDGE,"E52.1.0.0")}),1.0]])]});
            var Q9;
            Q9=makeQuery(id+"F5.imprint","IMPRINT",FACE,{"disambiguationData":[TD([[makeQuery(id+"F5.imprint","IMPRINT",EDGE,{"derivedFrom":sQuery(id+"F5.wireOp",EDGE,"E47")}),1.0]])]});
            var Q10;
            Q10=makeQuery(id+"F5.imprint","IMPRINT",FACE,{"disambiguationData":[TD([[makeQuery(id+"F5.imprint","IMPRINT",EDGE,{"derivedFrom":sQuery(id+"F5.wireOp",EDGE,"E41.MirrorCS")}),1.0]])]});
            var Q11;
            Q11=makeQuery(id+"F5.imprint","IMPRINT",FACE,{"disambiguationData":[TD([[makeQuery(id+"F5.imprint","IMPRINT",EDGE,{"derivedFrom":sQuery(id+"F5.wireOp",EDGE,"E36")}),-1.0]])]});
            extrude(context, id + "F11", {"entities" : qUnion([Q0, Q1, Q2, Q3, Q4, Q5, Q6, Q7, Q8, Q9, Q10, Q11]), "operationType" : NewBodyOperationType.REMOVE, "oppositeDirection" : true, "depth" : 1 * mm, "offsetDistance" : 25 * mm});
        }
        {
            var Q0;
            Q0=qCreatedBy(makeId("Right.planeOp"),FACE);
            var sketch = newSketch(context, id + "F12", { "sketchPlane" : qUnion([Q0])});
            skCircle(sketch, "E63", {"center": v(-5.3, -7.5) * mm, "radius": 1.25 * mm});
            skCircle(sketch, "E64", {"center": v(-54.7, -7.5) * mm, "radius": 1.25 * mm});
            skCircle(sketch, "E65", {"center": v(-5, 27.5) * mm, "radius": 1.6 * mm});
            skCircle(sketch, "E66", {"center": v(-55, 27.5) * mm, "radius": 1.6 * mm});
            skSolve(sketch);
        }
        {
            var Q0;
            Q0=makeQuery(id+"F12.imprint","IMPRINT",FACE,{"disambiguationData":[TD([[makeQuery(id+"F12.imprint","IMPRINT",EDGE,{"derivedFrom":sQuery(id+"F12.wireOp",EDGE,"E64")}),1.0]])]});
            var Q1;
            Q1=makeQuery(id+"F12.imprint","IMPRINT",FACE,{"disambiguationData":[TD([[makeQuery(id+"F12.imprint","IMPRINT",EDGE,{"derivedFrom":sQuery(id+"F12.wireOp",EDGE,"E63")}),1.0]])]});
            var Q2;
            Q2=makeQuery(id+"F12.imprint","IMPRINT",FACE,{"disambiguationData":[TD([[makeQuery(id+"F12.imprint","IMPRINT",EDGE,{"derivedFrom":sQuery(id+"F12.wireOp",EDGE,"E65")}),1.0]])]});
            var Q3;
            Q3=makeQuery(id+"F12.imprint","IMPRINT",FACE,{"disambiguationData":[TD([[makeQuery(id+"F12.imprint","IMPRINT",EDGE,{"derivedFrom":sQuery(id+"F12.wireOp",EDGE,"E66")}),1.0]])]});
            extrude(context, id + "F13", {"entities" : qUnion([Q0, Q1, Q2, Q3]), "operationType" : NewBodyOperationType.REMOVE, "depth" : getVariable(context, 'width') + getVariable(context, 'wallthickness'), "offsetDistance" : 25 * mm, "hasSecondDirection" : true, "secondDirectionOppositeDirection" : true, "secondDirectionDepth" : getVariable(context, 'wallthickness')});
        }
        {
            var Q0;
            Q0=qCreatedBy(makeId("Front.planeOp"),FACE);
            var sketch = newSketch(context, id + "F14", { "sketchPlane" : qUnion([Q0])});
            skLineSegment(sketch, "E67", {"start": v(4, 29) * mm, "end": v(6, 29) * mm});
            skLineSegment(sketch, "E68", {"start": v(6, 29) * mm, "end": v(6, 6) * mm});
            skLineSegment(sketch, "E69", {"start": v(6, 6) * mm, "end": v(4, 6) * mm});
            skLineSegment(sketch, "E70", {"start": v(4, 6) * mm, "end": v(4, 29) * mm});
            skLineSegment(sketch, "E71.1.0.0", {"start": v(10, 6) * mm, "end": v(8, 6) * mm});
            skLineSegment(sketch, "E71.1.0.1", {"start": v(8, 29) * mm, "end": v(10, 29) * mm});
            skLineSegment(sketch, "E71.1.0.2", {"start": v(8, 6) * mm, "end": v(8, 29) * mm});
            skLineSegment(sketch, "E71.1.0.3", {"start": v(10, 29) * mm, "end": v(10, 6) * mm});
            skLineSegment(sketch, "E71.2.0.0", {"start": v(14, 6) * mm, "end": v(12, 6) * mm});
            skLineSegment(sketch, "E71.2.0.1", {"start": v(12, 29) * mm, "end": v(14, 29) * mm});
            skLineSegment(sketch, "E71.2.0.2", {"start": v(12, 6) * mm, "end": v(12, 29) * mm});
            skLineSegment(sketch, "E71.2.0.3", {"start": v(14, 29) * mm, "end": v(14, 6) * mm});
            skLineSegment(sketch, "E71.3.0.0", {"start": v(18, 6) * mm, "end": v(16, 6) * mm});
            skLineSegment(sketch, "E71.3.0.1", {"start": v(16, 29) * mm, "end": v(18, 29) * mm});
            skLineSegment(sketch, "E71.3.0.2", {"start": v(16, 6) * mm, "end": v(16, 29) * mm});
            skLineSegment(sketch, "E71.3.0.3", {"start": v(18, 29) * mm, "end": v(18, 6) * mm});
            skLineSegment(sketch, "E71.4.0.0", {"start": v(22, 6) * mm, "end": v(20, 6) * mm});
            skLineSegment(sketch, "E71.4.0.1", {"start": v(20, 29) * mm, "end": v(22, 29) * mm});
            skLineSegment(sketch, "E71.4.0.2", {"start": v(20, 6) * mm, "end": v(20, 29) * mm});
            skLineSegment(sketch, "E71.4.0.3", {"start": v(22, 29) * mm, "end": v(22, 6) * mm});
            skLineSegment(sketch, "E71.5.0.0", {"start": v(26, 6) * mm, "end": v(24, 6) * mm});
            skLineSegment(sketch, "E71.5.0.1", {"start": v(24, 29) * mm, "end": v(26, 29) * mm});
            skLineSegment(sketch, "E71.5.0.2", {"start": v(24, 6) * mm, "end": v(24, 29) * mm});
            skLineSegment(sketch, "E71.5.0.3", {"start": v(26, 29) * mm, "end": v(26, 6) * mm});
            skLineSegment(sketch, "E71.6.0.0", {"start": v(30, 6) * mm, "end": v(28, 6) * mm});
            skLineSegment(sketch, "E71.6.0.1", {"start": v(28, 29) * mm, "end": v(30, 29) * mm});
            skLineSegment(sketch, "E71.6.0.2", {"start": v(28, 6) * mm, "end": v(28, 29) * mm});
            skLineSegment(sketch, "E71.6.0.3", {"start": v(30, 29) * mm, "end": v(30, 6) * mm});
            skLineSegment(sketch, "E71.7.0.0", {"start": v(34, 6) * mm, "end": v(32, 6) * mm});
            skLineSegment(sketch, "E71.7.0.1", {"start": v(32, 29) * mm, "end": v(34, 29) * mm});
            skLineSegment(sketch, "E71.7.0.2", {"start": v(32, 6) * mm, "end": v(32, 29) * mm});
            skLineSegment(sketch, "E71.7.0.3", {"start": v(34, 29) * mm, "end": v(34, 6) * mm});
            skLineSegment(sketch, "E71.8.0.0", {"start": v(38, 6) * mm, "end": v(36, 6) * mm});
            skLineSegment(sketch, "E71.8.0.1", {"start": v(36, 29) * mm, "end": v(38, 29) * mm});
            skLineSegment(sketch, "E71.8.0.2", {"start": v(36, 6) * mm, "end": v(36, 29) * mm});
            skLineSegment(sketch, "E71.8.0.3", {"start": v(38, 29) * mm, "end": v(38, 6) * mm});
            skLineSegment(sketch, "E71.9.0.0", {"start": v(42, 6) * mm, "end": v(40, 6) * mm});
            skLineSegment(sketch, "E71.9.0.1", {"start": v(40, 29) * mm, "end": v(42, 29) * mm});
            skLineSegment(sketch, "E71.9.0.2", {"start": v(40, 6) * mm, "end": v(40, 29) * mm});
            skLineSegment(sketch, "E71.9.0.3", {"start": v(42, 29) * mm, "end": v(42, 6) * mm});
            skLineSegment(sketch, "E71.10.0.0", {"start": v(46, 6) * mm, "end": v(44, 6) * mm});
            skLineSegment(sketch, "E71.10.0.1", {"start": v(44, 29) * mm, "end": v(46, 29) * mm});
            skLineSegment(sketch, "E71.10.0.2", {"start": v(44, 6) * mm, "end": v(44, 29) * mm});
            skLineSegment(sketch, "E71.10.0.3", {"start": v(46, 29) * mm, "end": v(46, 6) * mm});
            skLineSegment(sketch, "E71.11.0.0", {"start": v(50, 6) * mm, "end": v(48, 6) * mm});
            skLineSegment(sketch, "E71.11.0.1", {"start": v(48, 29) * mm, "end": v(50, 29) * mm});
            skLineSegment(sketch, "E71.11.0.2", {"start": v(48, 6) * mm, "end": v(48, 29) * mm});
            skLineSegment(sketch, "E71.11.0.3", {"start": v(50, 29) * mm, "end": v(50, 6) * mm});
            skLineSegment(sketch, "E71.12.0.0", {"start": v(54, 6) * mm, "end": v(52, 6) * mm});
            skLineSegment(sketch, "E71.12.0.1", {"start": v(52, 29) * mm, "end": v(54, 29) * mm});
            skLineSegment(sketch, "E71.12.0.2", {"start": v(52, 6) * mm, "end": v(52, 29) * mm});
            skLineSegment(sketch, "E71.12.0.3", {"start": v(54, 29) * mm, "end": v(54, 6) * mm});
            skLineSegment(sketch, "E71.13.0.0", {"start": v(58, 6) * mm, "end": v(56, 6) * mm});
            skLineSegment(sketch, "E71.13.0.1", {"start": v(56, 29) * mm, "end": v(58, 29) * mm});
            skLineSegment(sketch, "E71.13.0.2", {"start": v(56, 6) * mm, "end": v(56, 29) * mm});
            skLineSegment(sketch, "E71.13.0.3", {"start": v(58, 29) * mm, "end": v(58, 6) * mm});
            skLineSegment(sketch, "E71.14.0.0", {"start": v(62, 6) * mm, "end": v(60, 6) * mm});
            skLineSegment(sketch, "E71.14.0.1", {"start": v(60, 29) * mm, "end": v(62, 29) * mm});
            skLineSegment(sketch, "E71.14.0.2", {"start": v(60, 6) * mm, "end": v(60, 29) * mm});
            skLineSegment(sketch, "E71.14.0.3", {"start": v(62, 29) * mm, "end": v(62, 6) * mm});
            skLineSegment(sketch, "E71.15.0.0", {"start": v(66, 6) * mm, "end": v(64, 6) * mm});
            skLineSegment(sketch, "E71.15.0.1", {"start": v(64, 29) * mm, "end": v(66, 29) * mm});
            skLineSegment(sketch, "E71.15.0.2", {"start": v(64, 6) * mm, "end": v(64, 29) * mm});
            skLineSegment(sketch, "E71.15.0.3", {"start": v(66, 29) * mm, "end": v(66, 6) * mm});
            skLineSegment(sketch, "E71.16.0.0", {"start": v(70, 6) * mm, "end": v(68, 6) * mm});
            skLineSegment(sketch, "E71.16.0.1", {"start": v(68, 29) * mm, "end": v(70, 29) * mm});
            skLineSegment(sketch, "E71.16.0.2", {"start": v(68, 6) * mm, "end": v(68, 29) * mm});
            skLineSegment(sketch, "E71.16.0.3", {"start": v(70, 29) * mm, "end": v(70, 6) * mm});
            skLineSegment(sketch, "E71.17.0.0", {"start": v(74, 6) * mm, "end": v(72, 6) * mm});
            skLineSegment(sketch, "E71.17.0.1", {"start": v(72, 29) * mm, "end": v(74, 29) * mm});
            skLineSegment(sketch, "E71.17.0.2", {"start": v(72, 6) * mm, "end": v(72, 29) * mm});
            skLineSegment(sketch, "E71.17.0.3", {"start": v(74, 29) * mm, "end": v(74, 6) * mm});
            skLineSegment(sketch, "E71.18.0.0", {"start": v(78, 6) * mm, "end": v(76, 6) * mm});
            skLineSegment(sketch, "E71.18.0.1", {"start": v(76, 29) * mm, "end": v(78, 29) * mm});
            skLineSegment(sketch, "E71.18.0.2", {"start": v(76, 6) * mm, "end": v(76, 29) * mm});
            skLineSegment(sketch, "E71.18.0.3", {"start": v(78, 29) * mm, "end": v(78, 6) * mm});
            skLineSegment(sketch, "E71.direction1", {"start": v(4, 6) * mm, "end": v(8, 6) * mm, "construction": true});
            skSolve(sketch);
        }
        {
            var Q0;
            Q0=makeQuery(id+"F14.imprint","IMPRINT",FACE,{"disambiguationData":[TD([[makeQuery(id+"F14.imprint","IMPRINT",EDGE,{"derivedFrom":sQuery(id+"F14.wireOp",EDGE,"E67")}),-1.0]])]});
            var Q1;
            Q1=makeQuery(id+"F14.imprint","IMPRINT",FACE,{"disambiguationData":[TD([[makeQuery(id+"F14.imprint","IMPRINT",EDGE,{"derivedFrom":sQuery(id+"F14.wireOp",EDGE,"E71.1.0.0")}),-1.0]])]});
            var Q2;
            Q2=makeQuery(id+"F14.imprint","IMPRINT",FACE,{"disambiguationData":[TD([[makeQuery(id+"F14.imprint","IMPRINT",EDGE,{"derivedFrom":sQuery(id+"F14.wireOp",EDGE,"E71.2.0.0")}),-1.0]])]});
            var Q3;
            Q3=makeQuery(id+"F14.imprint","IMPRINT",FACE,{"disambiguationData":[TD([[makeQuery(id+"F14.imprint","IMPRINT",EDGE,{"derivedFrom":sQuery(id+"F14.wireOp",EDGE,"E71.3.0.0")}),-1.0]])]});
            var Q4;
            Q4=makeQuery(id+"F14.imprint","IMPRINT",FACE,{"disambiguationData":[TD([[makeQuery(id+"F14.imprint","IMPRINT",EDGE,{"derivedFrom":sQuery(id+"F14.wireOp",EDGE,"E71.4.0.0")}),-1.0]])]});
            var Q5;
            Q5=makeQuery(id+"F14.imprint","IMPRINT",FACE,{"disambiguationData":[TD([[makeQuery(id+"F14.imprint","IMPRINT",EDGE,{"derivedFrom":sQuery(id+"F14.wireOp",EDGE,"E71.5.0.0")}),-1.0]])]});
            var Q6;
            Q6=makeQuery(id+"F14.imprint","IMPRINT",FACE,{"disambiguationData":[TD([[makeQuery(id+"F14.imprint","IMPRINT",EDGE,{"derivedFrom":sQuery(id+"F14.wireOp",EDGE,"E71.6.0.0")}),-1.0]])]});
            var Q7;
            Q7=makeQuery(id+"F14.imprint","IMPRINT",FACE,{"disambiguationData":[TD([[makeQuery(id+"F14.imprint","IMPRINT",EDGE,{"derivedFrom":sQuery(id+"F14.wireOp",EDGE,"E71.7.0.0")}),-1.0]])]});
            var Q8;
            Q8=makeQuery(id+"F14.imprint","IMPRINT",FACE,{"disambiguationData":[TD([[makeQuery(id+"F14.imprint","IMPRINT",EDGE,{"derivedFrom":sQuery(id+"F14.wireOp",EDGE,"E71.8.0.0")}),-1.0]])]});
            var Q9;
            Q9=makeQuery(id+"F14.imprint","IMPRINT",FACE,{"disambiguationData":[TD([[makeQuery(id+"F14.imprint","IMPRINT",EDGE,{"derivedFrom":sQuery(id+"F14.wireOp",EDGE,"E71.9.0.0")}),-1.0]])]});
            var Q10;
            Q10=makeQuery(id+"F14.imprint","IMPRINT",FACE,{"disambiguationData":[TD([[makeQuery(id+"F14.imprint","IMPRINT",EDGE,{"derivedFrom":sQuery(id+"F14.wireOp",EDGE,"E71.10.0.0")}),-1.0]])]});
            var Q11;
            Q11=makeQuery(id+"F14.imprint","IMPRINT",FACE,{"disambiguationData":[TD([[makeQuery(id+"F14.imprint","IMPRINT",EDGE,{"derivedFrom":sQuery(id+"F14.wireOp",EDGE,"E71.11.0.0")}),-1.0]])]});
            var Q12;
            Q12=makeQuery(id+"F14.imprint","IMPRINT",FACE,{"disambiguationData":[TD([[makeQuery(id+"F14.imprint","IMPRINT",EDGE,{"derivedFrom":sQuery(id+"F14.wireOp",EDGE,"E71.12.0.0")}),-1.0]])]});
            var Q13;
            Q13=makeQuery(id+"F14.imprint","IMPRINT",FACE,{"disambiguationData":[TD([[makeQuery(id+"F14.imprint","IMPRINT",EDGE,{"derivedFrom":sQuery(id+"F14.wireOp",EDGE,"E71.13.0.0")}),-1.0]])]});
            var Q14;
            Q14=makeQuery(id+"F14.imprint","IMPRINT",FACE,{"disambiguationData":[TD([[makeQuery(id+"F14.imprint","IMPRINT",EDGE,{"derivedFrom":sQuery(id+"F14.wireOp",EDGE,"E71.14.0.0")}),-1.0]])]});
            var Q15;
            Q15=makeQuery(id+"F14.imprint","IMPRINT",FACE,{"disambiguationData":[TD([[makeQuery(id+"F14.imprint","IMPRINT",EDGE,{"derivedFrom":sQuery(id+"F14.wireOp",EDGE,"E71.15.0.0")}),-1.0]])]});
            var Q16;
            Q16=makeQuery(id+"F14.imprint","IMPRINT",FACE,{"disambiguationData":[TD([[makeQuery(id+"F14.imprint","IMPRINT",EDGE,{"derivedFrom":sQuery(id+"F14.wireOp",EDGE,"E71.16.0.0")}),-1.0]])]});
            var Q17;
            Q17=makeQuery(id+"F14.imprint","IMPRINT",FACE,{"disambiguationData":[TD([[makeQuery(id+"F14.imprint","IMPRINT",EDGE,{"derivedFrom":sQuery(id+"F14.wireOp",EDGE,"E71.17.0.0")}),-1.0]])]});
            var Q18;
            Q18=makeQuery(id+"F14.imprint","IMPRINT",FACE,{"disambiguationData":[TD([[makeQuery(id+"F14.imprint","IMPRINT",EDGE,{"derivedFrom":sQuery(id+"F14.wireOp",EDGE,"E71.18.0.0")}),-1.0]])]});
            extrude(context, id + "F15", {"entities" : qUnion([Q0, Q1, Q2, Q3, Q4, Q5, Q6, Q7, Q8, Q9, Q10, Q11, Q12, Q13, Q14, Q15, Q16, Q17, Q18]), "operationType" : NewBodyOperationType.REMOVE, "oppositeDirection" : true, "depth" : getVariable(context, 'wallthickness'), "offsetDistance" : 25 * mm, "hasSecondDirection" : true, "secondDirectionOppositeDirection" : false, "secondDirectionDepth" : getVariable(context, 'height') + getVariable(context, 'wallthickness')});
        }
        {
            var Q0;
            Q0=makeQuery(id+"F6.opExtrude","SWEPT_FACE",FACE,{"disambiguationData":[OSD([sQuery(id+"F5.wireOp",EDGE,"E4.1")])]});
            var Q1;
            Q1=makeQuery(id+"F7.boolean.opBoolean","MERGE",FACE,{"derivedFrom":[makeQuery(id+"F6.opExtrude","SWEPT_FACE",FACE,{"disambiguationData":[OSD([sQuery(id+"F5.wireOp",EDGE,"E4.0")])]}),makeQuery(id+"F7.opExtrude","SWEPT_FACE",FACE,{"disambiguationData":[OSD([sQuery(id+"F5.wireOp",EDGE,"E53")])]}),makeQuery(id+"F7.opExtrude","SWEPT_FACE",FACE,{"disambiguationData":[OSD([sQuery(id+"F5.wireOp",EDGE,"E61.MirrorCS")])]})]});
            var Q2;
            Q2=makeQuery(id+"F6.opExtrude","SWEPT_FACE",FACE,{"disambiguationData":[OSD([sQuery(id+"F5.wireOp",EDGE,"E4.2")])]});
            var Q3;
            Q3=makeQuery(id+"F6.opExtrude","SWEPT_FACE",FACE,{"disambiguationData":[OSD([sQuery(id+"F5.wireOp",EDGE,"E4.3")])]});
            var Q4;
            {var subQ0=sQuery(id+"F5.wireOp",EDGE,"E4.3");var subQ1=sQuery(id+"F5.wireOp",EDGE,"E4.1");var subQ2=sQuery(id+"F5.wireOp",EDGE,"E3");var subQ3=sQuery(id+"F5.wireOp",EDGE,"E2");var subQ4=sQuery(id+"F5.wireOp",EDGE,"E1");var subQ5=sQuery(id+"F5.wireOp",EDGE,"E0");Q4=makeQuery(id+"F7.boolean.opBoolean","MERGE",FACE,{"derivedFrom":[makeQuery(id+"F6.opExtrude","CAP_FACE",FACE,{"disambiguationData":[OSD([subQ5,subQ4,subQ3,subQ2,sQuery(id+"F5.wireOp",EDGE,"E4.0"),subQ1,sQuery(id+"F5.wireOp",EDGE,"E4.2"),subQ0])],"isStart":true}),makeQuery(id+"F7.opExtrude","CAP_FACE",FACE,{"disambiguationData":[OSD([subQ5,subQ4,subQ3,subQ2])],"isStart":true}),makeQuery(id+"F7.opExtrude","CAP_FACE",FACE,{"disambiguationData":[OSD([subQ1,sQuery(id+"F5.wireOp",EDGE,"E53"),sQuery(id+"F5.wireOp",EDGE,"E55"),sQuery(id+"F5.wireOp",EDGE,"E56"),sQuery(id+"F5.wireOp",EDGE,"E57")])],"isStart":true}),makeQuery(id+"F7.opExtrude","CAP_FACE",FACE,{"disambiguationData":[OSD([subQ0,sQuery(id+"F5.wireOp",EDGE,"E58.MirrorC"),sQuery(id+"F5.wireOp",EDGE,"E59.MirrorCS"),sQuery(id+"F5.wireOp",EDGE,"E60.MirrorCS"),sQuery(id+"F5.wireOp",EDGE,"E61.MirrorCS")])],"isStart":true})]});}
            var Q5;
            Q5=makeQuery(id+"F7.opExtrude","CAP_FACE",FACE,{"disambiguationData":[OSD([sQuery(id+"F5.wireOp",EDGE,"E0"),sQuery(id+"F5.wireOp",EDGE,"E1"),sQuery(id+"F5.wireOp",EDGE,"E2"),sQuery(id+"F5.wireOp",EDGE,"E3")])],"isStart":false});
            var Q6;
            Q6=makeQuery(id+"F6.opExtrude","SWEPT_FACE",FACE,{"disambiguationData":[OSD([sQuery(id+"F5.wireOp",EDGE,"E3")])]});
            var Q7;
            Q7=makeQuery(id+"F6.opExtrude","SWEPT_FACE",FACE,{"disambiguationData":[OSD([sQuery(id+"F5.wireOp",EDGE,"E1")])]});
            var Q8;
            Q8=makeQuery(id+"F6.opExtrude","SWEPT_FACE",FACE,{"disambiguationData":[OSD([sQuery(id+"F5.wireOp",EDGE,"E0")])]});
            var Q9;
            Q9=makeQuery(id+"F6.opExtrude","SWEPT_FACE",FACE,{"disambiguationData":[OSD([sQuery(id+"F5.wireOp",EDGE,"E2")])]});
            var Q10;
            Q10=makeQuery(id+"F8.opExtrude","CAP_FACE",FACE,{"disambiguationData":[OSD([sQuery(id+"F5.wireOp",EDGE,"E4.0"),sQuery(id+"F5.wireOp",EDGE,"E4.1"),sQuery(id+"F5.wireOp",EDGE,"E4.2"),sQuery(id+"F5.wireOp",EDGE,"E4.3"),sQuery(id+"F5.wireOp",EDGE,"E15"),sQuery(id+"F5.wireOp",EDGE,"E16"),sQuery(id+"F5.wireOp",EDGE,"E17"),sQuery(id+"F5.wireOp",EDGE,"E18"),sQuery(id+"F5.wireOp",EDGE,"E19"),sQuery(id+"F5.wireOp",EDGE,"E21.MirrorCS"),sQuery(id+"F5.wireOp",EDGE,"E22.MirrorCS"),sQuery(id+"F5.wireOp",EDGE,"E23.MirrorCS"),sQuery(id+"F5.wireOp",EDGE,"E24.MirrorCS"),sQuery(id+"F5.wireOp",EDGE,"E25.1.0.0"),sQuery(id+"F5.wireOp",EDGE,"E25.1.0.1"),sQuery(id+"F5.wireOp",EDGE,"E25.1.0.2"),sQuery(id+"F5.wireOp",EDGE,"E25.1.0.3"),sQuery(id+"F5.wireOp",EDGE,"E25.1.0.4"),sQuery(id+"F5.wireOp",EDGE,"E25.1.0.5"),sQuery(id+"F5.wireOp",EDGE,"E25.1.0.6"),sQuery(id+"F5.wireOp",EDGE,"E25.1.0.7"),sQuery(id+"F5.wireOp",EDGE,"E25.1.0.9"),sQuery(id+"F5.wireOp",EDGE,"E25.2.0.0"),sQuery(id+"F5.wireOp",EDGE,"E25.2.0.1"),sQuery(id+"F5.wireOp",EDGE,"E25.2.0.2"),sQuery(id+"F5.wireOp",EDGE,"E25.2.0.3"),sQuery(id+"F5.wireOp",EDGE,"E25.2.0.4"),sQuery(id+"F5.wireOp",EDGE,"E25.2.0.5"),sQuery(id+"F5.wireOp",EDGE,"E25.2.0.6"),sQuery(id+"F5.wireOp",EDGE,"E25.2.0.7"),sQuery(id+"F5.wireOp",EDGE,"E25.2.0.9"),sQuery(id+"F5.wireOp",EDGE,"E25.3.0.0"),sQuery(id+"F5.wireOp",EDGE,"E25.3.0.1"),sQuery(id+"F5.wireOp",EDGE,"E25.3.0.2"),sQuery(id+"F5.wireOp",EDGE,"E25.3.0.3"),sQuery(id+"F5.wireOp",EDGE,"E25.3.0.4"),sQuery(id+"F5.wireOp",EDGE,"E25.3.0.5"),sQuery(id+"F5.wireOp",EDGE,"E25.3.0.6"),sQuery(id+"F5.wireOp",EDGE,"E25.3.0.7"),sQuery(id+"F5.wireOp",EDGE,"E25.3.0.9")])],"isStart":false});
            var Q11;
            {var subQ0=sQuery(id+"F5.wireOp",EDGE,"E25.3.0.9");var subQ1=sQuery(id+"F5.wireOp",EDGE,"E25.3.0.7");var subQ2=sQuery(id+"F5.wireOp",EDGE,"E25.3.0.6");var subQ3=sQuery(id+"F5.wireOp",EDGE,"E25.3.0.4");var subQ4=sQuery(id+"F5.wireOp",EDGE,"E25.3.0.3");var subQ5=sQuery(id+"F5.wireOp",EDGE,"E25.3.0.2");var subQ6=sQuery(id+"F5.wireOp",EDGE,"E25.3.0.1");var subQ7=sQuery(id+"F5.wireOp",EDGE,"E25.3.0.0");var subQ8=sQuery(id+"F5.wireOp",EDGE,"E25.2.0.9");var subQ9=sQuery(id+"F5.wireOp",EDGE,"E25.2.0.7");var subQ10=sQuery(id+"F5.wireOp",EDGE,"E25.2.0.6");var subQ11=sQuery(id+"F5.wireOp",EDGE,"E25.2.0.4");var subQ12=sQuery(id+"F5.wireOp",EDGE,"E25.2.0.3");var subQ13=sQuery(id+"F5.wireOp",EDGE,"E25.2.0.2");var subQ14=sQuery(id+"F5.wireOp",EDGE,"E25.2.0.1");var subQ15=sQuery(id+"F5.wireOp",EDGE,"E25.2.0.0");var subQ16=sQuery(id+"F5.wireOp",EDGE,"E25.1.0.9");var subQ17=sQuery(id+"F5.wireOp",EDGE,"E25.1.0.7");var subQ18=sQuery(id+"F5.wireOp",EDGE,"E25.1.0.6");var subQ19=sQuery(id+"F5.wireOp",EDGE,"E25.1.0.4");var subQ20=sQuery(id+"F5.wireOp",EDGE,"E25.1.0.3");var subQ21=sQuery(id+"F5.wireOp",EDGE,"E25.1.0.2");var subQ22=sQuery(id+"F5.wireOp",EDGE,"E25.1.0.1");var subQ23=sQuery(id+"F5.wireOp",EDGE,"E25.1.0.0");var subQ24=sQuery(id+"F5.wireOp",EDGE,"E24.MirrorCS");var subQ25=sQuery(id+"F5.wireOp",EDGE,"E23.MirrorCS");var subQ26=sQuery(id+"F5.wireOp",EDGE,"E22.MirrorCS");var subQ27=sQuery(id+"F5.wireOp",EDGE,"E21.MirrorCS");var subQ28=sQuery(id+"F5.wireOp",EDGE,"E19");var subQ29=sQuery(id+"F5.wireOp",EDGE,"E18");var subQ30=sQuery(id+"F5.wireOp",EDGE,"E17");var subQ31=sQuery(id+"F5.wireOp",EDGE,"E16");Q11=makeQuery(id+"F9.boolean.opBoolean","MERGE",FACE,{"derivedFrom":[makeQuery(id+"F8.opExtrude","CAP_FACE",FACE,{"disambiguationData":[OSD([sQuery(id+"F5.wireOp",EDGE,"E4.0"),sQuery(id+"F5.wireOp",EDGE,"E4.1"),sQuery(id+"F5.wireOp",EDGE,"E4.2"),sQuery(id+"F5.wireOp",EDGE,"E4.3"),sQuery(id+"F5.wireOp",EDGE,"E15"),subQ31,subQ30,subQ29,subQ28,subQ27,subQ26,subQ25,subQ24,subQ23,subQ22,subQ21,subQ20,subQ19,sQuery(id+"F5.wireOp",EDGE,"E25.1.0.5"),subQ18,subQ17,subQ16,subQ15,subQ14,subQ13,subQ12,subQ11,sQuery(id+"F5.wireOp",EDGE,"E25.2.0.5"),subQ10,subQ9,subQ8,subQ7,subQ6,subQ5,subQ4,subQ3,sQuery(id+"F5.wireOp",EDGE,"E25.3.0.5"),subQ2,subQ1,subQ0])],"isStart":true}),makeQuery(id+"F9.opExtrude","CAP_FACE",FACE,{"disambiguationData":[OSD([subQ31,subQ30,subQ29,subQ28])],"isStart":true}),makeQuery(id+"F9.opExtrude","CAP_FACE",FACE,{"disambiguationData":[OSD([subQ27,subQ26,subQ25,subQ24])],"isStart":true}),makeQuery(id+"F9.opExtrude","CAP_FACE",FACE,{"disambiguationData":[OSD([subQ23,subQ22,subQ21,subQ20])],"isStart":true}),makeQuery(id+"F9.opExtrude","CAP_FACE",FACE,{"disambiguationData":[OSD([subQ19,subQ18,subQ17,subQ16])],"isStart":true}),makeQuery(id+"F9.opExtrude","CAP_FACE",FACE,{"disambiguationData":[OSD([subQ15,subQ14,subQ13,subQ12])],"isStart":true}),makeQuery(id+"F9.opExtrude","CAP_FACE",FACE,{"disambiguationData":[OSD([subQ11,subQ10,subQ9,subQ8])],"isStart":true}),makeQuery(id+"F9.opExtrude","CAP_FACE",FACE,{"disambiguationData":[OSD([subQ7,subQ6,subQ5,subQ4])],"isStart":true}),makeQuery(id+"F9.opExtrude","CAP_FACE",FACE,{"disambiguationData":[OSD([subQ3,subQ2,subQ1,subQ0])],"isStart":true})]});}
            var Q12;
            Q12=makeQuery(id+"F10.opExtrude","SWEPT_FACE",FACE,{"disambiguationData":[OSD([sQuery(id+"F5.wireOp",EDGE,"E27.MirrorCS")])]});
            var Q13;
            Q13=makeQuery(id+"F10.opExtrude","SWEPT_FACE",FACE,{"disambiguationData":[OSD([sQuery(id+"F5.wireOp",EDGE,"E31.MirrorCS")])]});
            var Q14;
            Q14=makeQuery(id+"F10.opExtrude","SWEPT_FACE",FACE,{"disambiguationData":[OSD([sQuery(id+"F5.wireOp",EDGE,"E6")])]});
            var Q15;
            Q15=makeQuery(id+"F10.opExtrude","SWEPT_FACE",FACE,{"disambiguationData":[OSD([sQuery(id+"F5.wireOp",EDGE,"E10.MirrorCS")])]});
            var Q16;
            Q16=makeQuery(id+"F10.opExtrude","SWEPT_FACE",FACE,{"disambiguationData":[OSD([sQuery(id+"F5.wireOp",EDGE,"E13.MirrorCS")])]});
            var Q17;
            Q17=makeQuery(id+"F10.opExtrude","SWEPT_FACE",FACE,{"disambiguationData":[OSD([sQuery(id+"F5.wireOp",EDGE,"E8")])]});
            var Q18;
            Q18=makeQuery(id+"F10.opExtrude","SWEPT_FACE",FACE,{"disambiguationData":[OSD([sQuery(id+"F5.wireOp",EDGE,"E30.MirrorCS")])]});
            var Q19;
            Q19=makeQuery(id+"F10.opExtrude","SWEPT_FACE",FACE,{"disambiguationData":[OSD([sQuery(id+"F5.wireOp",EDGE,"E32.MirrorCS")])]});
            var Q20;
            Q20=makeQuery(id+"F10.opExtrude","CAP_FACE",FACE,{"disambiguationData":[OSD([sQuery(id+"F5.wireOp",EDGE,"E10.MirrorCS"),sQuery(id+"F5.wireOp",EDGE,"E11.MirrorCS"),sQuery(id+"F5.wireOp",EDGE,"E12.MirrorCS"),sQuery(id+"F5.wireOp",EDGE,"E13.MirrorCS")])],"isStart":false});
            var Q21;
            Q21=makeQuery(id+"F10.opExtrude","CAP_FACE",FACE,{"disambiguationData":[OSD([sQuery(id+"F5.wireOp",EDGE,"E5"),sQuery(id+"F5.wireOp",EDGE,"E6"),sQuery(id+"F5.wireOp",EDGE,"E7"),sQuery(id+"F5.wireOp",EDGE,"E8")])],"isStart":false});
            var Q22;
            Q22=makeQuery(id+"F10.opExtrude","CAP_FACE",FACE,{"disambiguationData":[OSD([sQuery(id+"F5.wireOp",EDGE,"E31.MirrorCS"),sQuery(id+"F5.wireOp",EDGE,"E32.MirrorCS"),sQuery(id+"F5.wireOp",EDGE,"E33.MirrorCS"),sQuery(id+"F5.wireOp",EDGE,"E34.MirrorCS")])],"isStart":false});
            var Q23;
            Q23=makeQuery(id+"F8.opExtrude","SWEPT_FACE",FACE,{"disambiguationData":[OSD([sQuery(id+"F5.wireOp",EDGE,"E4.0")])]});
            var Q24;
            Q24=makeQuery(id+"F8.opExtrude","SWEPT_FACE",FACE,{"disambiguationData":[OSD([sQuery(id+"F5.wireOp",EDGE,"E4.2")])]});
            var Q25;
            Q25=makeQuery(id+"F7.opExtrude","SWEPT_FACE",FACE,{"disambiguationData":[OSD([sQuery(id+"F5.wireOp",EDGE,"E58.MirrorC")])]});
            var Q26;
            Q26=makeQuery(id+"F7.opExtrude","SWEPT_FACE",FACE,{"disambiguationData":[OSD([sQuery(id+"F5.wireOp",EDGE,"E57")])]});
            fillet(context, id + "F16", {"entities" : qUnion([Q0, Q1, Q2, Q3, Q4, Q5, Q6, Q7, Q8, Q9, Q10, Q11, Q12, Q13, Q14, Q15, Q16, Q17, Q18, Q19, Q20, Q21, Q22, Q23, Q24, Q25, Q26]), "radius" : getVariable(context, 'filletrad'), "tangentPropagation" : true, "allowEdgeOverflow" : false});
        }
    });
